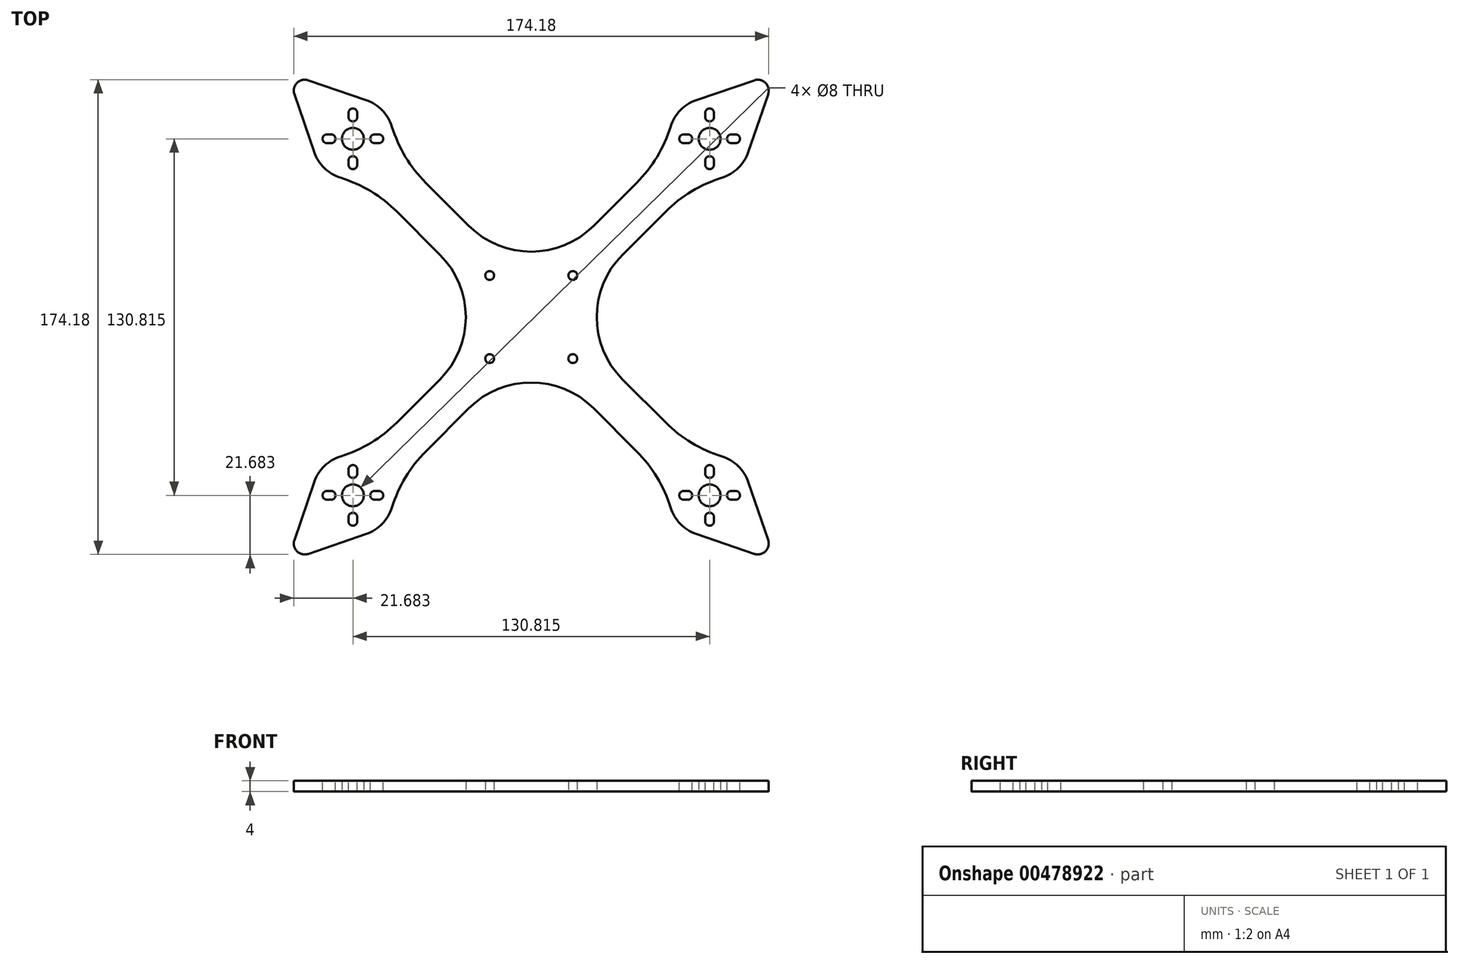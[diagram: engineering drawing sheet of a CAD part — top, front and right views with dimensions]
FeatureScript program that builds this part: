
annotation { "Feature Type Name" : "Feature", "Feature Type Description" : "" }
export const myFeature = defineFeature(function(context is Context, id is Id, definition is map)
    precondition{}
    {
        {
            var Q0;
            Q0=qCreatedBy(makeId("Top.planeOp"),FACE);
            var sketch = newSketch(context, id + "F0", { "sketchPlane" : qUnion([Q0])});
            skLineSegment(sketch, "E0", {"start": v(0, 0) * mm, "end": v(-65.4, 65.4) * mm, "construction": true});
            skArc(sketch, "E1", {"start": v(-51.08, 69.84) * mm, "mid": v(-54.65, 75.86) * mm, "end": v(-60.55, 79.6) * mm});
            skLineSegment(sketch, "E2", {"start": v(-38.67, 49.28) * mm, "end": v(-22.86, 33.47) * mm});
            skLineSegment(sketch, "E3", {"start": v(-49.28, 38.67) * mm, "end": v(-33.47, 22.86) * mm});
            skCircle(sketch, "E4", {"center": v(-15.25, 15.25) * mm, "radius": 1.63 * mm});
            skLineSegment(sketch, "E5.bottom", {"start": v(24, -24) * mm, "end": v(-24, -24) * mm, "construction": true});
            skLineSegment(sketch, "E5.top", {"start": v(24, 24) * mm, "end": v(-24, 24) * mm, "construction": true});
            skLineSegment(sketch, "E5.left", {"start": v(24, -24) * mm, "end": v(24, 24) * mm, "construction": true});
            skLineSegment(sketch, "E5.right", {"start": v(-24, -24) * mm, "end": v(-24, 24) * mm, "construction": true});
            skPoint(sketch, "E5.middle", {"position": v(0, 0) * mm});
            skArc(sketch, "E6", {"start": v(-24, 0) * mm, "mid": v(-26.46, 12.37) * mm, "end": v(-33.47, 22.86) * mm});
            skArc(sketch, "E7.MirrorCS", {"start": v(0, 24) * mm, "mid": v(-12.37, 26.46) * mm, "end": v(-22.86, 33.47) * mm});
            skLineSegment(sketch, "E8", {"start": v(-65.4, 65.4) * mm, "end": v(-83.09, 83.09) * mm, "construction": true});
            skArc(sketch, "E9", {"start": v(-81.79, 86.87) * mm, "mid": v(-85.91, 85.91) * mm, "end": v(-86.87, 81.79) * mm});
            skLineSegment(sketch, "E10", {"start": v(-86.87, 81.79) * mm, "end": v(-79.6, 60.55) * mm});
            skLineSegment(sketch, "E11", {"start": v(-81.79, 86.87) * mm, "end": v(-60.55, 79.6) * mm});
            skArc(sketch, "E12.trimOffspring", {"start": v(-79.6, 60.55) * mm, "mid": v(-75.86, 54.65) * mm, "end": v(-69.84, 51.08) * mm});
            skCircle(sketch, "E13", {"center": v(-65.4, 65.4) * mm, "radius": 4 * mm});
            skLineSegment(sketch, "E14", {"start": v(0, 0) * mm, "end": v(0, 24) * mm});
            skLineSegment(sketch, "E15", {"start": v(0, 0) * mm, "end": v(-24, 0) * mm});
            skArc(sketch, "E16", {"start": v(-51.08, 69.84) * mm, "mid": v(-46.13, 58.8) * mm, "end": v(-38.67, 49.28) * mm});
            skArc(sketch, "E17.MirrorCS", {"start": v(-69.84, 51.08) * mm, "mid": v(-58.8, 46.13) * mm, "end": v(-49.28, 38.67) * mm});
            skSolve(sketch);
        }
        {
            var Q0;
            Q0=makeQuery(id+"F0.imprint","IMPRINT",FACE,{"disambiguationData":[TD([[makeQuery(id+"F0.imprint","IMPRINT",EDGE,{"derivedFrom":sQuery(id+"F0.wireOp",EDGE,"E1")}),1.0]])]});
            extrude(context, id + "F1", {"entities" : qUnion([Q0]), "depth" : 4 * mm, "offsetDistance" : 25 * mm});
        }
        {
            var Q0;
            Q0=makeQuery(id+"F1.opExtrude","CAP_FACE",FACE,{"disambiguationData":[OSD([sQuery(id+"F0.wireOp",EDGE,"E1"),sQuery(id+"F0.wireOp",EDGE,"E2"),sQuery(id+"F0.wireOp",EDGE,"E3"),sQuery(id+"F0.wireOp",EDGE,"E4"),sQuery(id+"F0.wireOp",EDGE,"E6"),sQuery(id+"F0.wireOp",EDGE,"E7.MirrorCS"),sQuery(id+"F0.wireOp",EDGE,"E9"),sQuery(id+"F0.wireOp",EDGE,"E10"),sQuery(id+"F0.wireOp",EDGE,"E11"),sQuery(id+"F0.wireOp",EDGE,"E12.trimOffspring"),sQuery(id+"F0.wireOp",EDGE,"E13"),sQuery(id+"F0.wireOp",EDGE,"E14"),sQuery(id+"F0.wireOp",EDGE,"E15"),sQuery(id+"F0.wireOp",EDGE,"E16"),sQuery(id+"F0.wireOp",EDGE,"E17.MirrorCS")])],"isStart":false});
            var sketch = newSketch(context, id + "F2", { "sketchPlane" : qUnion([Q0])});
            skLineSegment(sketch, "E18", {"start": v(-57.4, 65.4) * mm, "end": v(-55.9, 65.4) * mm, "construction": true});
            skCircle(sketch, "E19", {"center": v(-65.4, 65.4) * mm, "radius": 8 * mm, "construction": true});
            skCircle(sketch, "E20", {"center": v(-65.4, 65.4) * mm, "radius": 9.5 * mm, "construction": true});
            skArc(sketch, "E21.0.startCap", {"start": v(-57.4, 63.78) * mm, "mid": v(-59.03, 65.4) * mm, "end": v(-57.4, 67.03) * mm});
            skArc(sketch, "E21.0.endCap", {"start": v(-55.9, 67.03) * mm, "mid": v(-54.28, 65.4) * mm, "end": v(-55.9, 63.78) * mm});
            skLineSegment(sketch, "E21.0.left", {"start": v(-57.4, 67.03) * mm, "end": v(-55.9, 67.03) * mm});
            skLineSegment(sketch, "E21.0.right", {"start": v(-57.4, 63.78) * mm, "end": v(-55.9, 63.78) * mm});
            skLineSegment(sketch, "E22.1.0", {"start": v(-65.4, 57.4) * mm, "end": v(-65.4, 55.9) * mm, "construction": true});
            skArc(sketch, "E22.1.1", {"start": v(-63.78, 55.9) * mm, "mid": v(-65.4, 54.28) * mm, "end": v(-67.03, 55.9) * mm});
            skArc(sketch, "E22.1.2", {"start": v(-67.03, 57.4) * mm, "mid": v(-65.4, 59.03) * mm, "end": v(-63.78, 57.4) * mm});
            skLineSegment(sketch, "E22.1.3", {"start": v(-63.78, 57.4) * mm, "end": v(-63.78, 55.9) * mm});
            skLineSegment(sketch, "E22.1.4", {"start": v(-67.03, 57.4) * mm, "end": v(-67.03, 55.9) * mm});
            skLineSegment(sketch, "E22.2.0", {"start": v(-73.4, 65.4) * mm, "end": v(-74.9, 65.4) * mm, "construction": true});
            skArc(sketch, "E22.2.1", {"start": v(-74.9, 63.78) * mm, "mid": v(-76.53, 65.4) * mm, "end": v(-74.9, 67.03) * mm});
            skArc(sketch, "E22.2.2", {"start": v(-73.4, 67.03) * mm, "mid": v(-71.78, 65.4) * mm, "end": v(-73.4, 63.78) * mm});
            skLineSegment(sketch, "E22.2.3", {"start": v(-73.4, 63.78) * mm, "end": v(-74.9, 63.78) * mm});
            skLineSegment(sketch, "E22.2.4", {"start": v(-73.4, 67.03) * mm, "end": v(-74.9, 67.03) * mm});
            skLineSegment(sketch, "E22.3.0", {"start": v(-65.4, 73.4) * mm, "end": v(-65.4, 74.9) * mm, "construction": true});
            skArc(sketch, "E22.3.1", {"start": v(-67.03, 74.9) * mm, "mid": v(-65.4, 76.53) * mm, "end": v(-63.78, 74.9) * mm});
            skArc(sketch, "E22.3.2", {"start": v(-63.78, 73.4) * mm, "mid": v(-65.4, 71.78) * mm, "end": v(-67.03, 73.4) * mm});
            skLineSegment(sketch, "E22.3.3", {"start": v(-67.03, 73.4) * mm, "end": v(-67.03, 74.9) * mm});
            skLineSegment(sketch, "E22.3.4", {"start": v(-63.78, 73.4) * mm, "end": v(-63.78, 74.9) * mm});
            skLineSegment(sketch, "E22.anchor1", {"start": v(-65.4, 65.4) * mm, "end": v(-57.4, 63.78) * mm, "construction": true});
            skLineSegment(sketch, "E22.anchor2", {"start": v(-65.4, 65.4) * mm, "end": v(-63.78, 73.4) * mm, "construction": true});
            skSolve(sketch);
        }
        {
            var Q0;
            Q0 = qSketchRegion(id + "F2", true);
            extrude(context, id + "F3", {"entities" : qUnion([Q0]), "operationType" : NewBodyOperationType.REMOVE, "oppositeDirection" : true, "depth" : 25 * mm, "offsetDistance" : 25 * mm});
        }
        {
            var Q0;
            Q0=makeQuery(id+"F1.opExtrude","SWEPT_BODY",BODY,{"disambiguationData":[OSD([sQuery(id+"F0.wireOp",EDGE,"E1"),sQuery(id+"F0.wireOp",EDGE,"E2"),sQuery(id+"F0.wireOp",EDGE,"E3"),sQuery(id+"F0.wireOp",EDGE,"E4"),sQuery(id+"F0.wireOp",EDGE,"E6"),sQuery(id+"F0.wireOp",EDGE,"E7.MirrorCS"),sQuery(id+"F0.wireOp",EDGE,"E9"),sQuery(id+"F0.wireOp",EDGE,"E10"),sQuery(id+"F0.wireOp",EDGE,"E11"),sQuery(id+"F0.wireOp",EDGE,"E12.trimOffspring"),sQuery(id+"F0.wireOp",EDGE,"E13"),sQuery(id+"F0.wireOp",EDGE,"E14"),sQuery(id+"F0.wireOp",EDGE,"E15")])]});
            var Q1;
            Q1=makeQuery(id+"F1.opExtrude","SWEPT_EDGE",EDGE,{"disambiguationData":[OSD([sQuery(id+"F0.wireOp",EDGE,"E14"),sQuery(id+"F0.wireOp",EDGE,"E15")])]});
            circularPattern(context, id + "F4", {"operationType" : NewBodyOperationType.ADD, "entities" : qUnion([Q0]), "axis" : qUnion([Q1]), "angle" : 360 * degree, "instanceCount" : 4, "equalSpace" : true});
        }
        {
            var Q0;
            Q0=makeQuery(id+"F4.boolean.opBoolean","MERGE",EDGE,{"derivedFrom":[makeQuery(id+"F4.opPattern","COPY",EDGE,{"derivedFrom":makeQuery(id+"F1.opExtrude","CAP_EDGE",EDGE,{"disambiguationData":[OSD([sQuery(id+"F0.wireOp",EDGE,"E7.MirrorCS")])],"isStart":false}),"instanceName":"2"}),makeQuery(id+"F4.opPattern","COPY",EDGE,{"derivedFrom":makeQuery(id+"F1.opExtrude","CAP_EDGE",EDGE,{"disambiguationData":[OSD([sQuery(id+"F0.wireOp",EDGE,"E6")])],"isStart":false}),"instanceName":"3"})]});
            var Q1;
            Q1=makeQuery(id+"F4.boolean.opBoolean","MERGE",EDGE,{"derivedFrom":[makeQuery(id+"F4.opPattern","COPY",EDGE,{"derivedFrom":makeQuery(id+"F1.opExtrude","CAP_EDGE",EDGE,{"disambiguationData":[OSD([sQuery(id+"F0.wireOp",EDGE,"E7.MirrorCS")])],"isStart":true}),"instanceName":"2"}),makeQuery(id+"F4.opPattern","COPY",EDGE,{"derivedFrom":makeQuery(id+"F1.opExtrude","CAP_EDGE",EDGE,{"disambiguationData":[OSD([sQuery(id+"F0.wireOp",EDGE,"E6")])],"isStart":true}),"instanceName":"3"})]});
            var Q2;
            Q2=makeQuery(id+"F4.opPattern","COPY",EDGE,{"derivedFrom":makeQuery(id+"F1.opExtrude","CAP_EDGE",EDGE,{"disambiguationData":[OSD([sQuery(id+"F0.wireOp",EDGE,"E4")])],"isStart":true}),"instanceName":"3"});
            var Q3;
            Q3=makeQuery(id+"F4.opPattern","COPY",EDGE,{"derivedFrom":makeQuery(id+"F1.opExtrude","CAP_EDGE",EDGE,{"disambiguationData":[OSD([sQuery(id+"F0.wireOp",EDGE,"E4")])],"isStart":true}),"instanceName":"2"});
            var Q4;
            Q4=makeQuery(id+"F1.opExtrude","CAP_EDGE",EDGE,{"disambiguationData":[OSD([sQuery(id+"F0.wireOp",EDGE,"E4")])],"isStart":true});
            var Q5;
            Q5=makeQuery(id+"F4.opPattern","COPY",EDGE,{"derivedFrom":makeQuery(id+"F1.opExtrude","CAP_EDGE",EDGE,{"disambiguationData":[OSD([sQuery(id+"F0.wireOp",EDGE,"E4")])],"isStart":true}),"instanceName":"1"});
            var Q6;
            Q6=makeQuery(id+"F4.opPattern","COPY",EDGE,{"derivedFrom":makeQuery(id+"F3.boolean.opBoolean","INTERSECT",EDGE,{"derivedFrom":[makeQuery(id+"F1.opExtrude","CAP_FACE",FACE,{"disambiguationData":[OSD([sQuery(id+"F0.wireOp",EDGE,"E1"),sQuery(id+"F0.wireOp",EDGE,"E2"),sQuery(id+"F0.wireOp",EDGE,"E3"),sQuery(id+"F0.wireOp",EDGE,"E4"),sQuery(id+"F0.wireOp",EDGE,"E6"),sQuery(id+"F0.wireOp",EDGE,"E7.MirrorCS"),sQuery(id+"F0.wireOp",EDGE,"E9"),sQuery(id+"F0.wireOp",EDGE,"E10"),sQuery(id+"F0.wireOp",EDGE,"E11"),sQuery(id+"F0.wireOp",EDGE,"E12.trimOffspring"),sQuery(id+"F0.wireOp",EDGE,"E13"),sQuery(id+"F0.wireOp",EDGE,"E14"),sQuery(id+"F0.wireOp",EDGE,"E15"),sQuery(id+"F0.wireOp",EDGE,"E16"),sQuery(id+"F0.wireOp",EDGE,"E17.MirrorCS")])],"isStart":true}),makeQuery(id+"F3.opExtrude","SWEPT_FACE",FACE,{"disambiguationData":[OSD([sQuery(id+"F2.wireOp",EDGE,"E21.0.right")])]})]}),"instanceName":"2"});
            var Q7;
            Q7=makeQuery(id+"F4.opPattern","COPY",EDGE,{"derivedFrom":makeQuery(id+"F3.boolean.opBoolean","INTERSECT",EDGE,{"derivedFrom":[makeQuery(id+"F1.opExtrude","CAP_FACE",FACE,{"disambiguationData":[OSD([sQuery(id+"F0.wireOp",EDGE,"E1"),sQuery(id+"F0.wireOp",EDGE,"E2"),sQuery(id+"F0.wireOp",EDGE,"E3"),sQuery(id+"F0.wireOp",EDGE,"E4"),sQuery(id+"F0.wireOp",EDGE,"E6"),sQuery(id+"F0.wireOp",EDGE,"E7.MirrorCS"),sQuery(id+"F0.wireOp",EDGE,"E9"),sQuery(id+"F0.wireOp",EDGE,"E10"),sQuery(id+"F0.wireOp",EDGE,"E11"),sQuery(id+"F0.wireOp",EDGE,"E12.trimOffspring"),sQuery(id+"F0.wireOp",EDGE,"E13"),sQuery(id+"F0.wireOp",EDGE,"E14"),sQuery(id+"F0.wireOp",EDGE,"E15"),sQuery(id+"F0.wireOp",EDGE,"E16"),sQuery(id+"F0.wireOp",EDGE,"E17.MirrorCS")])],"isStart":true}),makeQuery(id+"F3.opExtrude","SWEPT_FACE",FACE,{"disambiguationData":[OSD([sQuery(id+"F2.wireOp",EDGE,"E22.3.2")])]})]}),"instanceName":"2"});
            var Q8;
            Q8=makeQuery(id+"F4.opPattern","COPY",EDGE,{"derivedFrom":makeQuery(id+"F1.opExtrude","CAP_EDGE",EDGE,{"disambiguationData":[OSD([sQuery(id+"F0.wireOp",EDGE,"E13")])],"isStart":true}),"instanceName":"2"});
            var Q9;
            Q9=makeQuery(id+"F4.opPattern","COPY",EDGE,{"derivedFrom":makeQuery(id+"F3.boolean.opBoolean","INTERSECT",EDGE,{"derivedFrom":[makeQuery(id+"F1.opExtrude","CAP_FACE",FACE,{"disambiguationData":[OSD([sQuery(id+"F0.wireOp",EDGE,"E1"),sQuery(id+"F0.wireOp",EDGE,"E2"),sQuery(id+"F0.wireOp",EDGE,"E3"),sQuery(id+"F0.wireOp",EDGE,"E4"),sQuery(id+"F0.wireOp",EDGE,"E6"),sQuery(id+"F0.wireOp",EDGE,"E7.MirrorCS"),sQuery(id+"F0.wireOp",EDGE,"E9"),sQuery(id+"F0.wireOp",EDGE,"E10"),sQuery(id+"F0.wireOp",EDGE,"E11"),sQuery(id+"F0.wireOp",EDGE,"E12.trimOffspring"),sQuery(id+"F0.wireOp",EDGE,"E13"),sQuery(id+"F0.wireOp",EDGE,"E14"),sQuery(id+"F0.wireOp",EDGE,"E15"),sQuery(id+"F0.wireOp",EDGE,"E16"),sQuery(id+"F0.wireOp",EDGE,"E17.MirrorCS")])],"isStart":true}),makeQuery(id+"F3.opExtrude","SWEPT_FACE",FACE,{"disambiguationData":[OSD([sQuery(id+"F2.wireOp",EDGE,"E22.2.1")])]})]}),"instanceName":"2"});
            var Q10;
            Q10=makeQuery(id+"F4.opPattern","COPY",EDGE,{"derivedFrom":makeQuery(id+"F3.boolean.opBoolean","INTERSECT",EDGE,{"derivedFrom":[makeQuery(id+"F1.opExtrude","CAP_FACE",FACE,{"disambiguationData":[OSD([sQuery(id+"F0.wireOp",EDGE,"E1"),sQuery(id+"F0.wireOp",EDGE,"E2"),sQuery(id+"F0.wireOp",EDGE,"E3"),sQuery(id+"F0.wireOp",EDGE,"E4"),sQuery(id+"F0.wireOp",EDGE,"E6"),sQuery(id+"F0.wireOp",EDGE,"E7.MirrorCS"),sQuery(id+"F0.wireOp",EDGE,"E9"),sQuery(id+"F0.wireOp",EDGE,"E10"),sQuery(id+"F0.wireOp",EDGE,"E11"),sQuery(id+"F0.wireOp",EDGE,"E12.trimOffspring"),sQuery(id+"F0.wireOp",EDGE,"E13"),sQuery(id+"F0.wireOp",EDGE,"E14"),sQuery(id+"F0.wireOp",EDGE,"E15"),sQuery(id+"F0.wireOp",EDGE,"E16"),sQuery(id+"F0.wireOp",EDGE,"E17.MirrorCS")])],"isStart":true}),makeQuery(id+"F3.opExtrude","SWEPT_FACE",FACE,{"disambiguationData":[OSD([sQuery(id+"F2.wireOp",EDGE,"E22.1.1")])]})]}),"instanceName":"2"});
            var Q11;
            Q11=makeQuery(id+"F4.opPattern","COPY",EDGE,{"derivedFrom":makeQuery(id+"F3.boolean.opBoolean","INTERSECT",EDGE,{"derivedFrom":[makeQuery(id+"F1.opExtrude","CAP_FACE",FACE,{"disambiguationData":[OSD([sQuery(id+"F0.wireOp",EDGE,"E1"),sQuery(id+"F0.wireOp",EDGE,"E2"),sQuery(id+"F0.wireOp",EDGE,"E3"),sQuery(id+"F0.wireOp",EDGE,"E4"),sQuery(id+"F0.wireOp",EDGE,"E6"),sQuery(id+"F0.wireOp",EDGE,"E7.MirrorCS"),sQuery(id+"F0.wireOp",EDGE,"E9"),sQuery(id+"F0.wireOp",EDGE,"E10"),sQuery(id+"F0.wireOp",EDGE,"E11"),sQuery(id+"F0.wireOp",EDGE,"E12.trimOffspring"),sQuery(id+"F0.wireOp",EDGE,"E13"),sQuery(id+"F0.wireOp",EDGE,"E14"),sQuery(id+"F0.wireOp",EDGE,"E15"),sQuery(id+"F0.wireOp",EDGE,"E16"),sQuery(id+"F0.wireOp",EDGE,"E17.MirrorCS")])],"isStart":true}),makeQuery(id+"F3.opExtrude","SWEPT_FACE",FACE,{"disambiguationData":[OSD([sQuery(id+"F2.wireOp",EDGE,"E22.1.3")])]})]}),"instanceName":"3"});
            var Q12;
            Q12=makeQuery(id+"F4.opPattern","COPY",EDGE,{"derivedFrom":makeQuery(id+"F3.boolean.opBoolean","INTERSECT",EDGE,{"derivedFrom":[makeQuery(id+"F1.opExtrude","CAP_FACE",FACE,{"disambiguationData":[OSD([sQuery(id+"F0.wireOp",EDGE,"E1"),sQuery(id+"F0.wireOp",EDGE,"E2"),sQuery(id+"F0.wireOp",EDGE,"E3"),sQuery(id+"F0.wireOp",EDGE,"E4"),sQuery(id+"F0.wireOp",EDGE,"E6"),sQuery(id+"F0.wireOp",EDGE,"E7.MirrorCS"),sQuery(id+"F0.wireOp",EDGE,"E9"),sQuery(id+"F0.wireOp",EDGE,"E10"),sQuery(id+"F0.wireOp",EDGE,"E11"),sQuery(id+"F0.wireOp",EDGE,"E12.trimOffspring"),sQuery(id+"F0.wireOp",EDGE,"E13"),sQuery(id+"F0.wireOp",EDGE,"E14"),sQuery(id+"F0.wireOp",EDGE,"E15"),sQuery(id+"F0.wireOp",EDGE,"E16"),sQuery(id+"F0.wireOp",EDGE,"E17.MirrorCS")])],"isStart":true}),makeQuery(id+"F3.opExtrude","SWEPT_FACE",FACE,{"disambiguationData":[OSD([sQuery(id+"F2.wireOp",EDGE,"E22.2.2")])]})]}),"instanceName":"3"});
            var Q13;
            Q13=makeQuery(id+"F4.opPattern","COPY",EDGE,{"derivedFrom":makeQuery(id+"F1.opExtrude","CAP_EDGE",EDGE,{"disambiguationData":[OSD([sQuery(id+"F0.wireOp",EDGE,"E13")])],"isStart":true}),"instanceName":"3"});
            var Q14;
            Q14=makeQuery(id+"F4.opPattern","COPY",EDGE,{"derivedFrom":makeQuery(id+"F3.boolean.opBoolean","INTERSECT",EDGE,{"derivedFrom":[makeQuery(id+"F1.opExtrude","CAP_FACE",FACE,{"disambiguationData":[OSD([sQuery(id+"F0.wireOp",EDGE,"E1"),sQuery(id+"F0.wireOp",EDGE,"E2"),sQuery(id+"F0.wireOp",EDGE,"E3"),sQuery(id+"F0.wireOp",EDGE,"E4"),sQuery(id+"F0.wireOp",EDGE,"E6"),sQuery(id+"F0.wireOp",EDGE,"E7.MirrorCS"),sQuery(id+"F0.wireOp",EDGE,"E9"),sQuery(id+"F0.wireOp",EDGE,"E10"),sQuery(id+"F0.wireOp",EDGE,"E11"),sQuery(id+"F0.wireOp",EDGE,"E12.trimOffspring"),sQuery(id+"F0.wireOp",EDGE,"E13"),sQuery(id+"F0.wireOp",EDGE,"E14"),sQuery(id+"F0.wireOp",EDGE,"E15"),sQuery(id+"F0.wireOp",EDGE,"E16"),sQuery(id+"F0.wireOp",EDGE,"E17.MirrorCS")])],"isStart":true}),makeQuery(id+"F3.opExtrude","SWEPT_FACE",FACE,{"disambiguationData":[OSD([sQuery(id+"F2.wireOp",EDGE,"E22.3.4")])]})]}),"instanceName":"3"});
            var Q15;
            Q15=makeQuery(id+"F4.opPattern","COPY",EDGE,{"derivedFrom":makeQuery(id+"F3.boolean.opBoolean","INTERSECT",EDGE,{"derivedFrom":[makeQuery(id+"F1.opExtrude","CAP_FACE",FACE,{"disambiguationData":[OSD([sQuery(id+"F0.wireOp",EDGE,"E1"),sQuery(id+"F0.wireOp",EDGE,"E2"),sQuery(id+"F0.wireOp",EDGE,"E3"),sQuery(id+"F0.wireOp",EDGE,"E4"),sQuery(id+"F0.wireOp",EDGE,"E6"),sQuery(id+"F0.wireOp",EDGE,"E7.MirrorCS"),sQuery(id+"F0.wireOp",EDGE,"E9"),sQuery(id+"F0.wireOp",EDGE,"E10"),sQuery(id+"F0.wireOp",EDGE,"E11"),sQuery(id+"F0.wireOp",EDGE,"E12.trimOffspring"),sQuery(id+"F0.wireOp",EDGE,"E13"),sQuery(id+"F0.wireOp",EDGE,"E14"),sQuery(id+"F0.wireOp",EDGE,"E15"),sQuery(id+"F0.wireOp",EDGE,"E16"),sQuery(id+"F0.wireOp",EDGE,"E17.MirrorCS")])],"isStart":true}),makeQuery(id+"F3.opExtrude","SWEPT_FACE",FACE,{"disambiguationData":[OSD([sQuery(id+"F2.wireOp",EDGE,"E21.0.endCap")])]})]}),"instanceName":"3"});
            var Q16;
            Q16=makeQuery(id+"F3.boolean.opBoolean","INTERSECT",EDGE,{"derivedFrom":[makeQuery(id+"F1.opExtrude","CAP_FACE",FACE,{"disambiguationData":[OSD([sQuery(id+"F0.wireOp",EDGE,"E1"),sQuery(id+"F0.wireOp",EDGE,"E2"),sQuery(id+"F0.wireOp",EDGE,"E3"),sQuery(id+"F0.wireOp",EDGE,"E4"),sQuery(id+"F0.wireOp",EDGE,"E6"),sQuery(id+"F0.wireOp",EDGE,"E7.MirrorCS"),sQuery(id+"F0.wireOp",EDGE,"E9"),sQuery(id+"F0.wireOp",EDGE,"E10"),sQuery(id+"F0.wireOp",EDGE,"E11"),sQuery(id+"F0.wireOp",EDGE,"E12.trimOffspring"),sQuery(id+"F0.wireOp",EDGE,"E13"),sQuery(id+"F0.wireOp",EDGE,"E14"),sQuery(id+"F0.wireOp",EDGE,"E15"),sQuery(id+"F0.wireOp",EDGE,"E16"),sQuery(id+"F0.wireOp",EDGE,"E17.MirrorCS")])],"isStart":true}),makeQuery(id+"F3.opExtrude","SWEPT_FACE",FACE,{"disambiguationData":[OSD([sQuery(id+"F2.wireOp",EDGE,"E22.3.1")])]})]});
            var Q17;
            Q17=makeQuery(id+"F3.boolean.opBoolean","INTERSECT",EDGE,{"derivedFrom":[makeQuery(id+"F1.opExtrude","CAP_FACE",FACE,{"disambiguationData":[OSD([sQuery(id+"F0.wireOp",EDGE,"E1"),sQuery(id+"F0.wireOp",EDGE,"E2"),sQuery(id+"F0.wireOp",EDGE,"E3"),sQuery(id+"F0.wireOp",EDGE,"E4"),sQuery(id+"F0.wireOp",EDGE,"E6"),sQuery(id+"F0.wireOp",EDGE,"E7.MirrorCS"),sQuery(id+"F0.wireOp",EDGE,"E9"),sQuery(id+"F0.wireOp",EDGE,"E10"),sQuery(id+"F0.wireOp",EDGE,"E11"),sQuery(id+"F0.wireOp",EDGE,"E12.trimOffspring"),sQuery(id+"F0.wireOp",EDGE,"E13"),sQuery(id+"F0.wireOp",EDGE,"E14"),sQuery(id+"F0.wireOp",EDGE,"E15"),sQuery(id+"F0.wireOp",EDGE,"E16"),sQuery(id+"F0.wireOp",EDGE,"E17.MirrorCS")])],"isStart":true}),makeQuery(id+"F3.opExtrude","SWEPT_FACE",FACE,{"disambiguationData":[OSD([sQuery(id+"F2.wireOp",EDGE,"E21.0.startCap")])]})]});
            var Q18;
            Q18=makeQuery(id+"F3.boolean.opBoolean","INTERSECT",EDGE,{"derivedFrom":[makeQuery(id+"F1.opExtrude","CAP_FACE",FACE,{"disambiguationData":[OSD([sQuery(id+"F0.wireOp",EDGE,"E1"),sQuery(id+"F0.wireOp",EDGE,"E2"),sQuery(id+"F0.wireOp",EDGE,"E3"),sQuery(id+"F0.wireOp",EDGE,"E4"),sQuery(id+"F0.wireOp",EDGE,"E6"),sQuery(id+"F0.wireOp",EDGE,"E7.MirrorCS"),sQuery(id+"F0.wireOp",EDGE,"E9"),sQuery(id+"F0.wireOp",EDGE,"E10"),sQuery(id+"F0.wireOp",EDGE,"E11"),sQuery(id+"F0.wireOp",EDGE,"E12.trimOffspring"),sQuery(id+"F0.wireOp",EDGE,"E13"),sQuery(id+"F0.wireOp",EDGE,"E14"),sQuery(id+"F0.wireOp",EDGE,"E15"),sQuery(id+"F0.wireOp",EDGE,"E16"),sQuery(id+"F0.wireOp",EDGE,"E17.MirrorCS")])],"isStart":true}),makeQuery(id+"F3.opExtrude","SWEPT_FACE",FACE,{"disambiguationData":[OSD([sQuery(id+"F2.wireOp",EDGE,"E22.1.2")])]})]});
            var Q19;
            Q19=makeQuery(id+"F1.opExtrude","CAP_EDGE",EDGE,{"disambiguationData":[OSD([sQuery(id+"F0.wireOp",EDGE,"E13")])],"isStart":true});
            var Q20;
            Q20=makeQuery(id+"F3.boolean.opBoolean","INTERSECT",EDGE,{"derivedFrom":[makeQuery(id+"F1.opExtrude","CAP_FACE",FACE,{"disambiguationData":[OSD([sQuery(id+"F0.wireOp",EDGE,"E1"),sQuery(id+"F0.wireOp",EDGE,"E2"),sQuery(id+"F0.wireOp",EDGE,"E3"),sQuery(id+"F0.wireOp",EDGE,"E4"),sQuery(id+"F0.wireOp",EDGE,"E6"),sQuery(id+"F0.wireOp",EDGE,"E7.MirrorCS"),sQuery(id+"F0.wireOp",EDGE,"E9"),sQuery(id+"F0.wireOp",EDGE,"E10"),sQuery(id+"F0.wireOp",EDGE,"E11"),sQuery(id+"F0.wireOp",EDGE,"E12.trimOffspring"),sQuery(id+"F0.wireOp",EDGE,"E13"),sQuery(id+"F0.wireOp",EDGE,"E14"),sQuery(id+"F0.wireOp",EDGE,"E15"),sQuery(id+"F0.wireOp",EDGE,"E16"),sQuery(id+"F0.wireOp",EDGE,"E17.MirrorCS")])],"isStart":true}),makeQuery(id+"F3.opExtrude","SWEPT_FACE",FACE,{"disambiguationData":[OSD([sQuery(id+"F2.wireOp",EDGE,"E22.2.4")])]})]});
            var Q21;
            Q21=makeQuery(id+"F4.opPattern","COPY",EDGE,{"derivedFrom":makeQuery(id+"F3.boolean.opBoolean","INTERSECT",EDGE,{"derivedFrom":[makeQuery(id+"F1.opExtrude","CAP_FACE",FACE,{"disambiguationData":[OSD([sQuery(id+"F0.wireOp",EDGE,"E1"),sQuery(id+"F0.wireOp",EDGE,"E2"),sQuery(id+"F0.wireOp",EDGE,"E3"),sQuery(id+"F0.wireOp",EDGE,"E4"),sQuery(id+"F0.wireOp",EDGE,"E6"),sQuery(id+"F0.wireOp",EDGE,"E7.MirrorCS"),sQuery(id+"F0.wireOp",EDGE,"E9"),sQuery(id+"F0.wireOp",EDGE,"E10"),sQuery(id+"F0.wireOp",EDGE,"E11"),sQuery(id+"F0.wireOp",EDGE,"E12.trimOffspring"),sQuery(id+"F0.wireOp",EDGE,"E13"),sQuery(id+"F0.wireOp",EDGE,"E14"),sQuery(id+"F0.wireOp",EDGE,"E15"),sQuery(id+"F0.wireOp",EDGE,"E16"),sQuery(id+"F0.wireOp",EDGE,"E17.MirrorCS")])],"isStart":true}),makeQuery(id+"F3.opExtrude","SWEPT_FACE",FACE,{"disambiguationData":[OSD([sQuery(id+"F2.wireOp",EDGE,"E21.0.startCap")])]})]}),"instanceName":"1"});
            var Q22;
            Q22=makeQuery(id+"F4.opPattern","COPY",EDGE,{"derivedFrom":makeQuery(id+"F1.opExtrude","CAP_EDGE",EDGE,{"disambiguationData":[OSD([sQuery(id+"F0.wireOp",EDGE,"E13")])],"isStart":true}),"instanceName":"1"});
            var Q23;
            Q23=makeQuery(id+"F4.opPattern","COPY",EDGE,{"derivedFrom":makeQuery(id+"F3.boolean.opBoolean","INTERSECT",EDGE,{"derivedFrom":[makeQuery(id+"F1.opExtrude","CAP_FACE",FACE,{"disambiguationData":[OSD([sQuery(id+"F0.wireOp",EDGE,"E1"),sQuery(id+"F0.wireOp",EDGE,"E2"),sQuery(id+"F0.wireOp",EDGE,"E3"),sQuery(id+"F0.wireOp",EDGE,"E4"),sQuery(id+"F0.wireOp",EDGE,"E6"),sQuery(id+"F0.wireOp",EDGE,"E7.MirrorCS"),sQuery(id+"F0.wireOp",EDGE,"E9"),sQuery(id+"F0.wireOp",EDGE,"E10"),sQuery(id+"F0.wireOp",EDGE,"E11"),sQuery(id+"F0.wireOp",EDGE,"E12.trimOffspring"),sQuery(id+"F0.wireOp",EDGE,"E13"),sQuery(id+"F0.wireOp",EDGE,"E14"),sQuery(id+"F0.wireOp",EDGE,"E15"),sQuery(id+"F0.wireOp",EDGE,"E16"),sQuery(id+"F0.wireOp",EDGE,"E17.MirrorCS")])],"isStart":true}),makeQuery(id+"F3.opExtrude","SWEPT_FACE",FACE,{"disambiguationData":[OSD([sQuery(id+"F2.wireOp",EDGE,"E22.1.2")])]})]}),"instanceName":"1"});
            var Q24;
            Q24=makeQuery(id+"F4.opPattern","COPY",EDGE,{"derivedFrom":makeQuery(id+"F3.boolean.opBoolean","INTERSECT",EDGE,{"derivedFrom":[makeQuery(id+"F1.opExtrude","CAP_FACE",FACE,{"disambiguationData":[OSD([sQuery(id+"F0.wireOp",EDGE,"E1"),sQuery(id+"F0.wireOp",EDGE,"E2"),sQuery(id+"F0.wireOp",EDGE,"E3"),sQuery(id+"F0.wireOp",EDGE,"E4"),sQuery(id+"F0.wireOp",EDGE,"E6"),sQuery(id+"F0.wireOp",EDGE,"E7.MirrorCS"),sQuery(id+"F0.wireOp",EDGE,"E9"),sQuery(id+"F0.wireOp",EDGE,"E10"),sQuery(id+"F0.wireOp",EDGE,"E11"),sQuery(id+"F0.wireOp",EDGE,"E12.trimOffspring"),sQuery(id+"F0.wireOp",EDGE,"E13"),sQuery(id+"F0.wireOp",EDGE,"E14"),sQuery(id+"F0.wireOp",EDGE,"E15"),sQuery(id+"F0.wireOp",EDGE,"E16"),sQuery(id+"F0.wireOp",EDGE,"E17.MirrorCS")])],"isStart":true}),makeQuery(id+"F3.opExtrude","SWEPT_FACE",FACE,{"disambiguationData":[OSD([sQuery(id+"F2.wireOp",EDGE,"E22.2.3")])]})]}),"instanceName":"1"});
            var Q25;
            Q25=makeQuery(id+"F4.opPattern","COPY",EDGE,{"derivedFrom":makeQuery(id+"F3.boolean.opBoolean","INTERSECT",EDGE,{"derivedFrom":[makeQuery(id+"F1.opExtrude","CAP_FACE",FACE,{"disambiguationData":[OSD([sQuery(id+"F0.wireOp",EDGE,"E1"),sQuery(id+"F0.wireOp",EDGE,"E2"),sQuery(id+"F0.wireOp",EDGE,"E3"),sQuery(id+"F0.wireOp",EDGE,"E4"),sQuery(id+"F0.wireOp",EDGE,"E6"),sQuery(id+"F0.wireOp",EDGE,"E7.MirrorCS"),sQuery(id+"F0.wireOp",EDGE,"E9"),sQuery(id+"F0.wireOp",EDGE,"E10"),sQuery(id+"F0.wireOp",EDGE,"E11"),sQuery(id+"F0.wireOp",EDGE,"E12.trimOffspring"),sQuery(id+"F0.wireOp",EDGE,"E13"),sQuery(id+"F0.wireOp",EDGE,"E14"),sQuery(id+"F0.wireOp",EDGE,"E15"),sQuery(id+"F0.wireOp",EDGE,"E16"),sQuery(id+"F0.wireOp",EDGE,"E17.MirrorCS")])],"isStart":true}),makeQuery(id+"F3.opExtrude","SWEPT_FACE",FACE,{"disambiguationData":[OSD([sQuery(id+"F2.wireOp",EDGE,"E22.3.2")])]})]}),"instanceName":"1"});
            var Q26;
            Q26=makeQuery(id+"F4.opPattern","COPY",EDGE,{"derivedFrom":makeQuery(id+"F3.boolean.opBoolean","COPY",EDGE,{"derivedFrom":makeQuery(id+"F3.opExtrude","CAP_EDGE",EDGE,{"disambiguationData":[OSD([sQuery(id+"F2.wireOp",EDGE,"E21.0.startCap")])],"isStart":true})}),"instanceName":"1"});
            var Q27;
            Q27=makeQuery(id+"F4.opPattern","COPY",EDGE,{"derivedFrom":makeQuery(id+"F3.boolean.opBoolean","COPY",EDGE,{"derivedFrom":makeQuery(id+"F3.opExtrude","CAP_EDGE",EDGE,{"disambiguationData":[OSD([sQuery(id+"F2.wireOp",EDGE,"E22.1.2")])],"isStart":true})}),"instanceName":"1"});
            var Q28;
            Q28=makeQuery(id+"F4.opPattern","COPY",EDGE,{"derivedFrom":makeQuery(id+"F3.boolean.opBoolean","COPY",EDGE,{"derivedFrom":makeQuery(id+"F3.opExtrude","CAP_EDGE",EDGE,{"disambiguationData":[OSD([sQuery(id+"F2.wireOp",EDGE,"E22.3.2")])],"isStart":true})}),"instanceName":"1"});
            var Q29;
            Q29=makeQuery(id+"F4.opPattern","COPY",EDGE,{"derivedFrom":makeQuery(id+"F1.opExtrude","CAP_EDGE",EDGE,{"disambiguationData":[OSD([sQuery(id+"F0.wireOp",EDGE,"E13")])],"isStart":false}),"instanceName":"1"});
            var Q30;
            Q30=makeQuery(id+"F4.opPattern","COPY",EDGE,{"derivedFrom":makeQuery(id+"F3.boolean.opBoolean","COPY",EDGE,{"derivedFrom":makeQuery(id+"F3.opExtrude","CAP_EDGE",EDGE,{"disambiguationData":[OSD([sQuery(id+"F2.wireOp",EDGE,"E22.2.2")])],"isStart":true})}),"instanceName":"1"});
            var Q31;
            Q31=makeQuery(id+"F3.boolean.opBoolean","COPY",EDGE,{"derivedFrom":makeQuery(id+"F3.opExtrude","CAP_EDGE",EDGE,{"disambiguationData":[OSD([sQuery(id+"F2.wireOp",EDGE,"E22.1.2")])],"isStart":true})});
            var Q32;
            Q32=makeQuery(id+"F1.opExtrude","CAP_EDGE",EDGE,{"disambiguationData":[OSD([sQuery(id+"F0.wireOp",EDGE,"E13")])],"isStart":false});
            var Q33;
            Q33=makeQuery(id+"F3.boolean.opBoolean","COPY",EDGE,{"derivedFrom":makeQuery(id+"F3.opExtrude","CAP_EDGE",EDGE,{"disambiguationData":[OSD([sQuery(id+"F2.wireOp",EDGE,"E21.0.startCap")])],"isStart":true})});
            var Q34;
            Q34=makeQuery(id+"F3.boolean.opBoolean","COPY",EDGE,{"derivedFrom":makeQuery(id+"F3.opExtrude","CAP_EDGE",EDGE,{"disambiguationData":[OSD([sQuery(id+"F2.wireOp",EDGE,"E22.3.2")])],"isStart":true})});
            var Q35;
            Q35=makeQuery(id+"F3.boolean.opBoolean","COPY",EDGE,{"derivedFrom":makeQuery(id+"F3.opExtrude","CAP_EDGE",EDGE,{"disambiguationData":[OSD([sQuery(id+"F2.wireOp",EDGE,"E22.2.2")])],"isStart":true})});
            var Q36;
            Q36=makeQuery(id+"F4.opPattern","COPY",EDGE,{"derivedFrom":makeQuery(id+"F1.opExtrude","CAP_EDGE",EDGE,{"disambiguationData":[OSD([sQuery(id+"F0.wireOp",EDGE,"E4")])],"isStart":false}),"instanceName":"3"});
            var Q37;
            Q37=makeQuery(id+"F1.opExtrude","CAP_EDGE",EDGE,{"disambiguationData":[OSD([sQuery(id+"F0.wireOp",EDGE,"E4")])],"isStart":false});
            var Q38;
            Q38=makeQuery(id+"F4.opPattern","COPY",EDGE,{"derivedFrom":makeQuery(id+"F1.opExtrude","CAP_EDGE",EDGE,{"disambiguationData":[OSD([sQuery(id+"F0.wireOp",EDGE,"E4")])],"isStart":false}),"instanceName":"1"});
            var Q39;
            Q39=makeQuery(id+"F4.opPattern","COPY",EDGE,{"derivedFrom":makeQuery(id+"F1.opExtrude","CAP_EDGE",EDGE,{"disambiguationData":[OSD([sQuery(id+"F0.wireOp",EDGE,"E4")])],"isStart":false}),"instanceName":"2"});
            var Q40;
            Q40=makeQuery(id+"F4.opPattern","COPY",EDGE,{"derivedFrom":makeQuery(id+"F3.boolean.opBoolean","COPY",EDGE,{"derivedFrom":makeQuery(id+"F3.opExtrude","CAP_EDGE",EDGE,{"disambiguationData":[OSD([sQuery(id+"F2.wireOp",EDGE,"E22.3.1")])],"isStart":true})}),"instanceName":"3"});
            var Q41;
            Q41=makeQuery(id+"F4.opPattern","COPY",EDGE,{"derivedFrom":makeQuery(id+"F3.boolean.opBoolean","COPY",EDGE,{"derivedFrom":makeQuery(id+"F3.opExtrude","CAP_EDGE",EDGE,{"disambiguationData":[OSD([sQuery(id+"F2.wireOp",EDGE,"E21.0.left")])],"isStart":true})}),"instanceName":"3"});
            var Q42;
            Q42=makeQuery(id+"F4.opPattern","COPY",EDGE,{"derivedFrom":makeQuery(id+"F3.boolean.opBoolean","COPY",EDGE,{"derivedFrom":makeQuery(id+"F3.opExtrude","CAP_EDGE",EDGE,{"disambiguationData":[OSD([sQuery(id+"F2.wireOp",EDGE,"E22.1.2")])],"isStart":true})}),"instanceName":"3"});
            var Q43;
            Q43=makeQuery(id+"F4.opPattern","COPY",EDGE,{"derivedFrom":makeQuery(id+"F3.boolean.opBoolean","COPY",EDGE,{"derivedFrom":makeQuery(id+"F3.opExtrude","CAP_EDGE",EDGE,{"disambiguationData":[OSD([sQuery(id+"F2.wireOp",EDGE,"E22.2.2")])],"isStart":true})}),"instanceName":"3"});
            var Q44;
            Q44=makeQuery(id+"F4.opPattern","COPY",EDGE,{"derivedFrom":makeQuery(id+"F1.opExtrude","CAP_EDGE",EDGE,{"disambiguationData":[OSD([sQuery(id+"F0.wireOp",EDGE,"E13")])],"isStart":false}),"instanceName":"3"});
            var Q45;
            Q45=makeQuery(id+"F4.opPattern","COPY",EDGE,{"derivedFrom":makeQuery(id+"F3.boolean.opBoolean","COPY",EDGE,{"derivedFrom":makeQuery(id+"F3.opExtrude","CAP_EDGE",EDGE,{"disambiguationData":[OSD([sQuery(id+"F2.wireOp",EDGE,"E22.3.2")])],"isStart":true})}),"instanceName":"2"});
            var Q46;
            Q46=makeQuery(id+"F4.opPattern","COPY",EDGE,{"derivedFrom":makeQuery(id+"F3.boolean.opBoolean","COPY",EDGE,{"derivedFrom":makeQuery(id+"F3.opExtrude","CAP_EDGE",EDGE,{"disambiguationData":[OSD([sQuery(id+"F2.wireOp",EDGE,"E21.0.endCap")])],"isStart":true})}),"instanceName":"2"});
            var Q47;
            Q47=makeQuery(id+"F4.opPattern","COPY",EDGE,{"derivedFrom":makeQuery(id+"F1.opExtrude","CAP_EDGE",EDGE,{"disambiguationData":[OSD([sQuery(id+"F0.wireOp",EDGE,"E13")])],"isStart":false}),"instanceName":"2"});
            var Q48;
            Q48=makeQuery(id+"F4.opPattern","COPY",EDGE,{"derivedFrom":makeQuery(id+"F3.boolean.opBoolean","COPY",EDGE,{"derivedFrom":makeQuery(id+"F3.opExtrude","CAP_EDGE",EDGE,{"disambiguationData":[OSD([sQuery(id+"F2.wireOp",EDGE,"E22.1.3")])],"isStart":true})}),"instanceName":"2"});
            var Q49;
            Q49=makeQuery(id+"F4.opPattern","COPY",EDGE,{"derivedFrom":makeQuery(id+"F3.boolean.opBoolean","COPY",EDGE,{"derivedFrom":makeQuery(id+"F3.opExtrude","CAP_EDGE",EDGE,{"disambiguationData":[OSD([sQuery(id+"F2.wireOp",EDGE,"E22.2.2")])],"isStart":true})}),"instanceName":"2"});
            fillet(context, id + "F5", {"entities" : qUnion([Q0, Q1, Q2, Q3, Q4, Q5, Q6, Q7, Q8, Q9, Q10, Q11, Q12, Q13, Q14, Q15, Q16, Q17, Q18, Q19, Q20, Q21, Q22, Q23, Q24, Q25, Q26, Q27, Q28, Q29, Q30, Q31, Q32, Q33, Q34, Q35, Q36, Q37, Q38, Q39, Q40, Q41, Q42, Q43, Q44, Q45, Q46, Q47, Q48, Q49]), "radius" : .3 * mm, "tangentPropagation" : true, "allowEdgeOverflow" : false});
        }
    });
